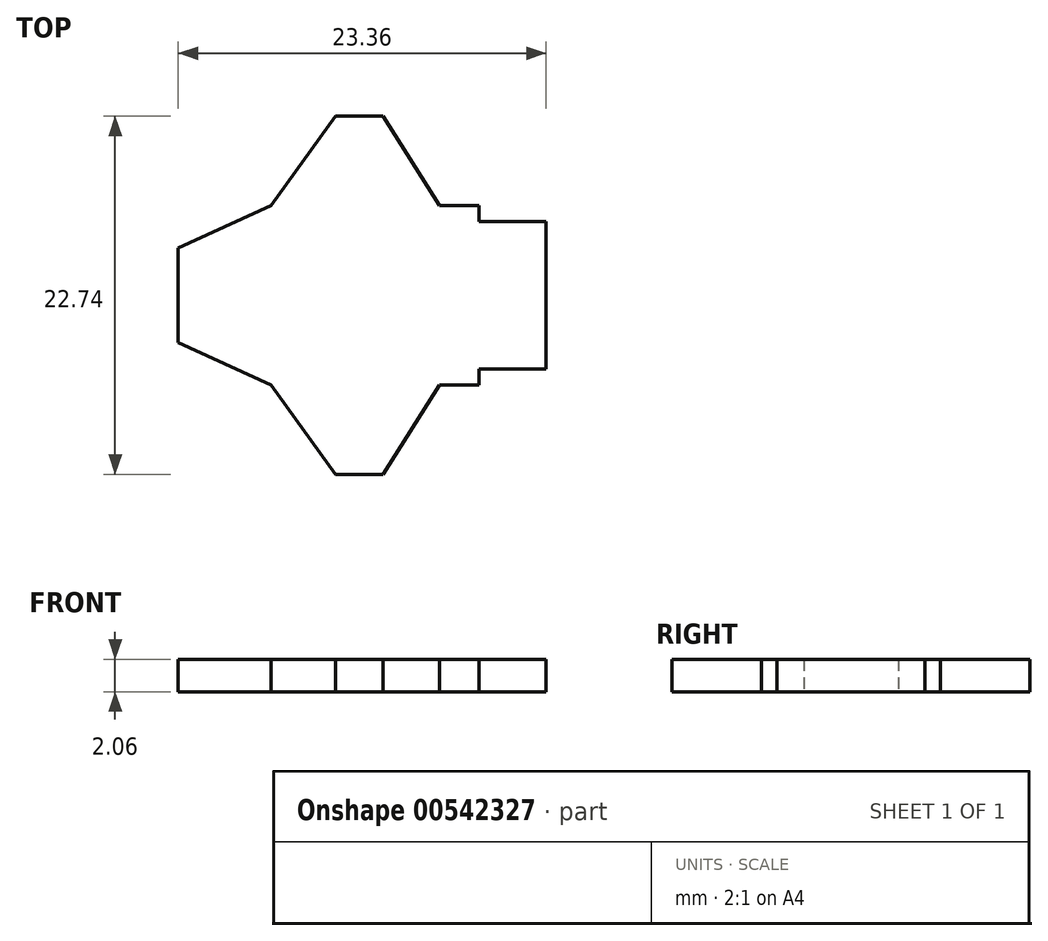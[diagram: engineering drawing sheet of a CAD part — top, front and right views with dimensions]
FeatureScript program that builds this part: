
annotation { "Feature Type Name" : "Feature", "Feature Type Description" : "" }
export const myFeature = defineFeature(function(context is Context, id is Id, definition is map)
    precondition{}
    {
        {
            var Q0;
            Q0=qCreatedBy(makeId("Top.planeOp"),FACE);
            var sketch = newSketch(context, id + "F0", { "sketchPlane" : qUnion([Q0])});
            skLineSegment(sketch, "E0", {"start": v(0, 0) * mm, "end": v(0, 3) * mm});
            skLineSegment(sketch, "E1", {"start": v(0, 3) * mm, "end": v(5.91, 5.7) * mm});
            skLineSegment(sketch, "E2", {"start": v(5.91, 5.7) * mm, "end": v(10, 11.37) * mm});
            skLineSegment(sketch, "E3", {"start": v(10, 11.37) * mm, "end": v(13, 11.37) * mm});
            skLineSegment(sketch, "E4", {"start": v(13, 11.37) * mm, "end": v(16.6, 5.7) * mm});
            skLineSegment(sketch, "E5", {"start": v(16.6, 5.7) * mm, "end": v(19.1, 5.7) * mm});
            skLineSegment(sketch, "E6", {"start": v(19.1, 5.7) * mm, "end": v(19.1, 4.7) * mm});
            skLineSegment(sketch, "E7", {"start": v(19.1, 4.7) * mm, "end": v(23.36, 4.7) * mm});
            skLineSegment(sketch, "E8", {"start": v(23.36, 4.7) * mm, "end": v(23.36, 0) * mm});
            skLineSegment(sketch, "E9.MirrorCS", {"start": v(19.1, -5.7) * mm, "end": v(19.1, -4.7) * mm});
            skLineSegment(sketch, "E10.MirrorCS", {"start": v(0, 0) * mm, "end": v(0, -3) * mm});
            skLineSegment(sketch, "E11.MirrorCS", {"start": v(0, -3) * mm, "end": v(5.91, -5.7) * mm});
            skLineSegment(sketch, "E12.MirrorCS", {"start": v(5.91, -5.7) * mm, "end": v(10, -11.37) * mm});
            skLineSegment(sketch, "E13.MirrorCS", {"start": v(10, -11.37) * mm, "end": v(13, -11.37) * mm});
            skLineSegment(sketch, "E14.MirrorCS", {"start": v(16.6, -5.7) * mm, "end": v(19.1, -5.7) * mm});
            skLineSegment(sketch, "E15.MirrorCS", {"start": v(13, -11.37) * mm, "end": v(16.6, -5.7) * mm});
            skLineSegment(sketch, "E16.MirrorCS", {"start": v(23.36, -4.7) * mm, "end": v(23.36, 0) * mm});
            skLineSegment(sketch, "E17.MirrorCS", {"start": v(19.1, -4.7) * mm, "end": v(23.36, -4.7) * mm});
            skSolve(sketch);
        }
        {
            var Q0;
            Q0=makeQuery(id+"F0.imprint","IMPRINT",FACE,{"disambiguationData":[TD([[makeQuery(id+"F0.imprint","IMPRINT",EDGE,{"derivedFrom":sQuery(id+"F0.wireOp",EDGE,"E0")}),-1.0]])]});
            extrude(context, id + "F1", {"entities" : qUnion([Q0]), "depth" : 2.06 * mm, "offsetDistance" : 25 * mm});
        }
    });
